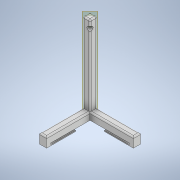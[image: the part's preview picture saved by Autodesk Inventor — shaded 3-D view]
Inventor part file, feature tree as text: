
AUTODESK INVENTOR PART (.ipt)
format: ipt  version: 2022 (Build 260153000, 153)  size: 183,808 bytes
history: native  units: mm
features: sketch x6, extrude x5, fillet x2, plane x1, hole x1
ambient origin geometry x8: Origin, YZ Plane, XZ Plane, XY Plane, X Axis, Y Axis, Z Axis, Center Point
bodies: Body1 (feature_tree)
feature tree (15):
  extrude  "Extrusion4"  Depth=25.0mm
  extrude  "Extrusion5"  Depth=25.0mm
  extrude  "Extrusion6"  Depth=25.0mm TaperAngle=0.0deg
  extrude  "Extrusion7"  Depth=25.0mm TaperAngle=0.0deg
  extrude  "Extrusion8"  Depth=85.0mm
  plane  "Work Plane2"
  hole  "Hole1"  [1 undecoded]
  fillet  "Fillet6"  Radius=85.0mm
  fillet  "Fillet7"  Radius=15.0mm
  sketch  "Sketch4"  dims[d16=25.0mm d17=300.0mm]
  sketch  "Sketch5"  dims[d18=25.0mm d19=0.0mm d20=25.0mm]
  sketch  "Sketch6"  dims[d21=25.0mm d22=150.0mm d23=0.0mm]
  sketch  "Sketch7"  dims[d24=150.0mm d25=0.0mm d30=25.0mm d31=0.0mm]
  sketch  "Sketch9"  dims[d32=8.5mm d33=85.0mm]
  sketch  "Sketch11"  dims[d34=100.0mm d37=3.5mm d40=85.0mm d41=15.0mm d42=8.5mm d43=3.5mm d44=25.0mm d45=0.0mm d47=15.0mm d48=6.0mm d49=4.0mm d50=2.0mm d51=90.0deg d52=8.0mm d53=20.594885mm d54=5.0mm d55=5.0mm]
note: 1 required parameter value undecoded (feature->parameter linkage not recoverable at this tier; creation-order binding heuristic only, values carry confidence <= 0.55)
